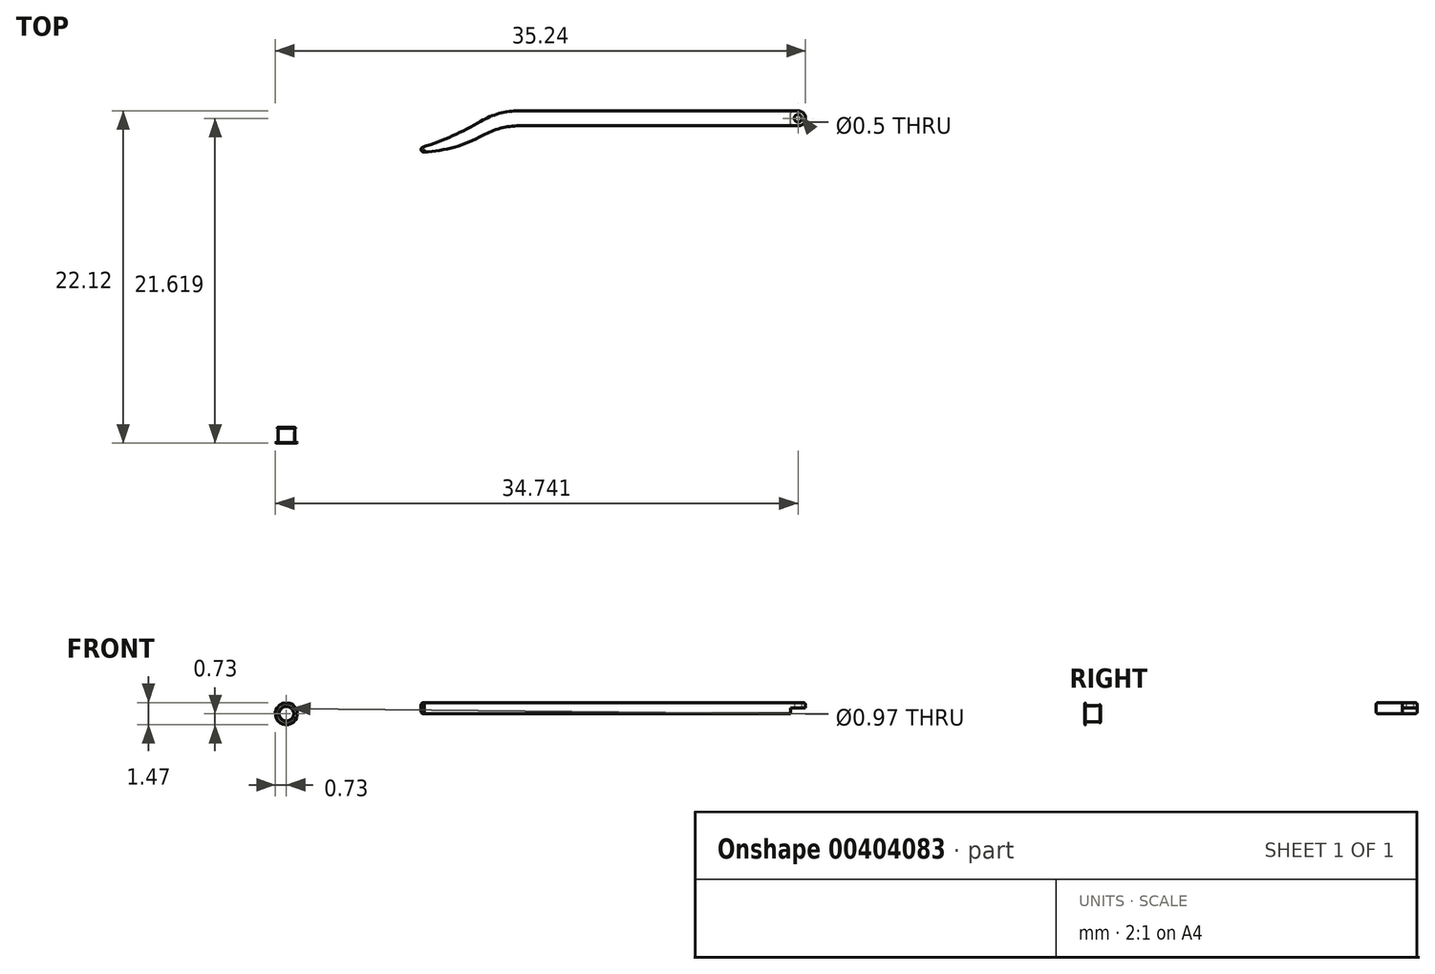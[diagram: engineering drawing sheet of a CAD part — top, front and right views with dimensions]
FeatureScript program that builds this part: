
annotation { "Feature Type Name" : "Feature", "Feature Type Description" : "" }
export const myFeature = defineFeature(function(context is Context, id is Id, definition is map)
    precondition{}
    {
        {
            var Q0;
            Q0=qCreatedBy(makeId("Top.planeOp"),FACE);
            var sketch = newSketch(context, id + "F0", { "sketchPlane" : qUnion([Q0])});
            skLineSegment(sketch, "E0", {"start": v(34.01, 20.71) * mm, "end": v(15.5, 20.71) * mm});
            skLineSegment(sketch, "E1", {"start": v(15.47, 21.7) * mm, "end": v(34.01, 21.7) * mm});
            skArc(sketch, "E2", {"start": v(9.08, 19.3) * mm, "mid": v(9.12, 19.31) * mm, "end": v(9.17, 19.33) * mm});
            skPoint(sketch, "E3.visualSharp", {"position": v(14.01, 21.7) * mm});
            skArc(sketch, "E3.filletArc", {"start": v(15.47, 21.7) * mm, "mid": v(14.15, 21.53) * mm, "end": v(12.92, 21) * mm});
            skArc(sketch, "E4", {"start": v(9.18, 18.97) * mm, "mid": v(11.18, 19.3) * mm, "end": v(13.06, 20.07) * mm});
            skArc(sketch, "E5.filletArc", {"start": v(15.5, 20.71) * mm, "mid": v(14.24, 20.55) * mm, "end": v(13.06, 20.07) * mm});
            skLineSegment(sketch, "E6", {"start": v(9.08, 19.3) * mm, "end": v(9.13, 19.13) * mm, "construction": true});
            skLineSegment(sketch, "E7", {"start": v(9.13, 19.13) * mm, "end": v(9.18, 18.97) * mm, "construction": true});
            skArc(sketch, "E8", {"start": v(34.01, 20.71) * mm, "mid": v(34.5, 21.2) * mm, "end": v(34.01, 21.7) * mm});
            skArc(sketch, "E9", {"start": v(9.08, 19.3) * mm, "mid": v(8.96, 19.08) * mm, "end": v(9.18, 18.97) * mm});
            skArc(sketch, "E10", {"start": v(9.17, 19.33) * mm, "mid": v(11.1, 20.06) * mm, "end": v(12.92, 21) * mm});
            skCircle(sketch, "E11", {"center": v(34.01, 21.2) * mm, "radius": 0.5 * mm});
            skPoint(sketch, "E12.trimOffspring.end.orphan", {"position": v(34.5, 21.2) * mm});
            skPoint(sketch, "E13.orphan", {"position": v(33.96, 21.7) * mm});
            skPoint(sketch, "E14.orphan", {"position": v(34.06, 21.7) * mm});
            skLineSegment(sketch, "E15", {"start": v(33.96, 21.16) * mm, "end": v(34.06, 21.16) * mm});
            skLineSegment(sketch, "E16", {"start": v(34.06, 21.16) * mm, "end": v(34.06, 21.26) * mm});
            skLineSegment(sketch, "E17", {"start": v(33.96, 21.16) * mm, "end": v(33.96, 21.26) * mm});
            skLineSegment(sketch, "E18", {"start": v(33.96, 21.26) * mm, "end": v(34.06, 21.26) * mm});
            skPoint(sketch, "E19", {"position": v(34.06, 21.26) * mm});
            skPoint(sketch, "E20", {"position": v(34.06, 21.16) * mm});
            skPoint(sketch, "E21", {"position": v(33.96, 21.16) * mm});
            skPoint(sketch, "E22", {"position": v(33.96, 21.26) * mm});
            skPoint(sketch, "E23.end.orphan", {"position": v(33.96, 21.1) * mm});
            skLineSegment(sketch, "E24", {"start": v(34.06, 21.26) * mm, "end": v(34.06, 21.53) * mm});
            skLineSegment(sketch, "E25", {"start": v(33.96, 21.26) * mm, "end": v(33.96, 21.53) * mm});
            skLineSegment(sketch, "E26", {"start": v(34.06, 21.26) * mm, "end": v(34.33, 21.26) * mm});
            skLineSegment(sketch, "E27", {"start": v(34.06, 21.16) * mm, "end": v(34.33, 21.16) * mm});
            skLineSegment(sketch, "E28", {"start": v(33.96, 21.16) * mm, "end": v(33.7, 21.16) * mm});
            skLineSegment(sketch, "E29", {"start": v(33.96, 21.26) * mm, "end": v(33.7, 21.26) * mm});
            skLineSegment(sketch, "E30", {"start": v(34.06, 21.16) * mm, "end": v(34.06, 20.89) * mm});
            skLineSegment(sketch, "E31", {"start": v(33.96, 21.16) * mm, "end": v(33.96, 20.89) * mm});
            skCircle(sketch, "E32", {"center": v(34.01, 21.2) * mm, "radius": 0.25 * mm});
            skCircle(sketch, "E33", {"center": v(34.01, 21.2) * mm, "radius": 0.32 * mm});
            skSolve(sketch);
        }
        {
            var Q0;
            {var subQ0=sQuery(id+"F0.wireOp",EDGE,"raI6fAfw-WQBC-BWmR-UYK9-M2oQmZqHLvwO");var subQ5=makeQuery(id+"F0.imprint","INTERSECT",VERTEX,{"derivedFrom":[subQ0,sQuery(id+"F0.wireOp",EDGE,"49f3884b-ec54-47d6-9d62-e5366d3701af.trimOffspring")]});Q0=makeQuery(id+"F0.imprint","IMPRINT",FACE,{"disambiguationData":[TD([[makeQuery(id+"F0.imprint","IMPRINT",EDGE,{"disambiguationData":[TD([[subQ5,-1.0]])],"derivedFrom":subQ0}),1.0]])]});}
            var Q1;
            {var subQ0=sQuery(id+"F0.wireOp",EDGE,"byHKuAPP-PSI1-Uxzz-RkZZ-SpkTKzF2PoQ2");Q1=makeQuery(id+"F0.imprint","IMPRINT",FACE,{"disambiguationData":[TD([[makeQuery(id+"F0.imprint","IMPRINT",EDGE,{"derivedFrom":subQ0}),1.0]])]});}
            var Q2;
            {var subQ0=sQuery(id+"F0.wireOp",EDGE,"byHKuAPP-PSI1-Uxzz-RkZZ-SpkTKzF2PoQ2");Q2=makeQuery(id+"F0.imprint","IMPRINT",FACE,{"disambiguationData":[TD([[makeQuery(id+"F0.imprint","IMPRINT",EDGE,{"derivedFrom":subQ0}),-1.0]])]});}
            var Q3;
            {var subQ0=sQuery(id+"F0.wireOp",EDGE,"b7881604-9c53-4a02-ad4f-a8e66866f7ef.trimOffspring");Q3=makeQuery(id+"F0.imprint","IMPRINT",FACE,{"disambiguationData":[TD([[makeQuery(id+"F0.imprint","IMPRINT",EDGE,{"derivedFrom":subQ0}),-1.0]])]});}
            var Q4;
            {var subQ0=sQuery(id+"F0.wireOp",EDGE,"f60c8f39-9fcf-4c3e-999d-d28395edd9ea.trimOffspring");Q4=makeQuery(id+"F0.imprint","IMPRINT",FACE,{"disambiguationData":[TD([[makeQuery(id+"F0.imprint","IMPRINT",EDGE,{"derivedFrom":subQ0}),-1.0]])]});}
            var Q5;
            {var subQ0=sQuery(id+"F0.wireOp",EDGE,"f60c8f39-9fcf-4c3e-999d-d28395edd9ea.trimOffspring");Q5=makeQuery(id+"F0.imprint","IMPRINT",FACE,{"disambiguationData":[TD([[makeQuery(id+"F0.imprint","IMPRINT",EDGE,{"derivedFrom":subQ0}),1.0]])]});}
            var Q6;
            {var subQ0=sQuery(id+"F0.wireOp",EDGE,"49f3884b-ec54-47d6-9d62-e5366d3701af.trimOffspring");Q6=makeQuery(id+"F0.imprint","IMPRINT",FACE,{"disambiguationData":[TD([[makeQuery(id+"F0.imprint","IMPRINT",EDGE,{"derivedFrom":subQ0}),1.0]])]});}
            var Q7;
            {var subQ0=sQuery(id+"F0.wireOp",EDGE,"UlwEkzhg-5pLx-n1i1-Rf2w-oDDQLxGLouVm");Q7=makeQuery(id+"F0.imprint","IMPRINT",FACE,{"disambiguationData":[TD([[makeQuery(id+"F0.imprint","IMPRINT",EDGE,{"derivedFrom":subQ0}),-1.0]])]});}
            var Q8;
            {var subQ0=sQuery(id+"F0.wireOp",EDGE,"UlwEkzhg-5pLx-n1i1-Rf2w-oDDQLxGLouVm");Q8=makeQuery(id+"F0.imprint","IMPRINT",FACE,{"disambiguationData":[TD([[makeQuery(id+"F0.imprint","IMPRINT",EDGE,{"derivedFrom":subQ0}),1.0]])]});}
            var Q9;
            {var subQ4=sQuery(id+"F0.wireOp",EDGE,"E11");var subQ5=makeQuery(id+"F0.imprint","INTERSECT",VERTEX,{"derivedFrom":[sQuery(id+"F0.wireOp",EDGE,"E0"),subQ4]});Q9=makeQuery(id+"F0.imprint","IMPRINT",FACE,{"disambiguationData":[TD([[makeQuery(id+"F0.imprint","IMPRINT",EDGE,{"disambiguationData":[TD([[subQ5,1.0]])],"derivedFrom":subQ4}),1.0]])]});}
            var Q10;
            {var subQ1=sQuery(id+"F0.wireOp",EDGE,"E0");Q10=makeQuery(id+"F0.imprint","IMPRINT",FACE,{"disambiguationData":[TD([[makeQuery(id+"F0.imprint","IMPRINT",EDGE,{"derivedFrom":subQ1}),-1.0]])]});}
            var Q11;
            Q11=makeQuery(id+"F0.imprint","IMPRINT",FACE,{"disambiguationData":[TD([[makeQuery(id+"F0.imprint","IMPRINT",EDGE,{"derivedFrom":sQuery(id+"F0.wireOp",EDGE,"xuiiaQj0-0Hdb-vT5L-Vz9f-apvYOn73sIt9")}),1.0]])]});
            var Q12;
            {var subQ0=sQuery(id+"F0.wireOp",EDGE,"8bITlogX-qrIG-J57A-UWLq-Q11sDlbSrRPg");Q12=makeQuery(id+"F0.imprint","IMPRINT",FACE,{"disambiguationData":[TD([[makeQuery(id+"F0.imprint","IMPRINT",EDGE,{"derivedFrom":subQ0}),1.0]])]});}
            var Q13;
            {var subQ2=sQuery(id+"F0.wireOp",EDGE,"CakERchI-l42z-6pcw-9BF8-LHwAbAGrC5tK");Q13=makeQuery(id+"F0.imprint","IMPRINT",FACE,{"disambiguationData":[TD([[makeQuery(id+"F0.imprint","IMPRINT",EDGE,{"derivedFrom":subQ2}),1.0]])]});}
            var Q14;
            {var subQ0=sQuery(id+"F0.wireOp",EDGE,"wC2ZcHAF-Bbkc-jGNR-qgdj-bPsWVvPjC4N5");Q14=makeQuery(id+"F0.imprint","IMPRINT",FACE,{"disambiguationData":[TD([[makeQuery(id+"F0.imprint","IMPRINT",EDGE,{"derivedFrom":subQ0}),1.0]])]});}
            var Q15;
            {var subQ2=sQuery(id+"F0.wireOp",EDGE,"E23");Q15=makeQuery(id+"F0.imprint","IMPRINT",FACE,{"disambiguationData":[TD([[makeQuery(id+"F0.imprint","IMPRINT",EDGE,{"derivedFrom":subQ2}),1.0]])]});}
            var Q16;
            {var subQ0=sQuery(id+"F0.wireOp",EDGE,"j64aIYXc-tMoq-sI7k-U2CT-7rPPRVJO4i3e");Q16=makeQuery(id+"F0.imprint","IMPRINT",FACE,{"disambiguationData":[TD([[makeQuery(id+"F0.imprint","IMPRINT",EDGE,{"derivedFrom":subQ0}),1.0]])]});}
            var Q17;
            {var subQ2=sQuery(id+"F0.wireOp",EDGE,"j64aIYXc-tMoq-sI7k-U2CT-7rPPRVJO4i3e");Q17=makeQuery(id+"F0.imprint","IMPRINT",FACE,{"disambiguationData":[TD([[makeQuery(id+"F0.imprint","IMPRINT",EDGE,{"derivedFrom":subQ2}),-1.0]])]});}
            var Q18;
            {var subQ0=sQuery(id+"F0.wireOp",EDGE,"GzgODX0R-oJ5M-ROGA-YiOL-rSwiiqXDl5Cg");Q18=makeQuery(id+"F0.imprint","IMPRINT",FACE,{"disambiguationData":[TD([[makeQuery(id+"F0.imprint","IMPRINT",EDGE,{"derivedFrom":subQ0}),-1.0]])]});}
            var Q19;
            {var subQ0=sQuery(id+"F0.wireOp",EDGE,"E28");var subQ1=sQuery(id+"F0.wireOp",EDGE,"E11");var subQ2=makeQuery(id+"F0.imprint","INTERSECT",VERTEX,{"derivedFrom":[subQ1,subQ0]});Q19=makeQuery(id+"F0.imprint","IMPRINT",FACE,{"disambiguationData":[TD([[makeQuery(id+"F0.imprint","IMPRINT",EDGE,{"disambiguationData":[TD([[subQ2,-1.0]])],"derivedFrom":subQ1}),1.0]])]});}
            var Q20;
            {var subQ0=sQuery(id+"F0.wireOp",EDGE,"E28");var subQ1=sQuery(id+"F0.wireOp",EDGE,"E11");var subQ2=makeQuery(id+"F0.imprint","INTERSECT",VERTEX,{"derivedFrom":[subQ1,subQ0]});Q20=makeQuery(id+"F0.imprint","IMPRINT",FACE,{"disambiguationData":[TD([[makeQuery(id+"F0.imprint","IMPRINT",EDGE,{"disambiguationData":[TD([[subQ2,1.0]])],"derivedFrom":subQ1}),1.0]])]});}
            var Q21;
            {var subQ0=sQuery(id+"F0.wireOp",EDGE,"E25");var subQ1=sQuery(id+"F0.wireOp",EDGE,"E11");var subQ2=makeQuery(id+"F0.imprint","INTERSECT",VERTEX,{"derivedFrom":[subQ1,subQ0]});Q21=makeQuery(id+"F0.imprint","IMPRINT",FACE,{"disambiguationData":[TD([[makeQuery(id+"F0.imprint","IMPRINT",EDGE,{"disambiguationData":[TD([[subQ2,-1.0]])],"derivedFrom":subQ1}),1.0]])]});}
            var Q22;
            {var subQ0=sQuery(id+"F0.wireOp",EDGE,"E25");var subQ1=sQuery(id+"F0.wireOp",EDGE,"kEdUQFwA-TB42-oZai-H7MF-9FTqb3vRD3eQ");var subQ2=makeQuery(id+"F0.imprint","INTERSECT",VERTEX,{"derivedFrom":[subQ1,subQ0]});Q22=makeQuery(id+"F0.imprint","IMPRINT",FACE,{"disambiguationData":[TD([[makeQuery(id+"F0.imprint","IMPRINT",EDGE,{"disambiguationData":[TD([[subQ2,-1.0]])],"derivedFrom":subQ1}),-1.0]])]});}
            var Q23;
            {var subQ0=sQuery(id+"F0.wireOp",EDGE,"E29");var subQ1=sQuery(id+"F0.wireOp",EDGE,"kEdUQFwA-TB42-oZai-H7MF-9FTqb3vRD3eQ");var subQ2=makeQuery(id+"F0.imprint","INTERSECT",VERTEX,{"derivedFrom":[subQ1,subQ0]});Q23=makeQuery(id+"F0.imprint","IMPRINT",FACE,{"disambiguationData":[TD([[makeQuery(id+"F0.imprint","IMPRINT",EDGE,{"disambiguationData":[TD([[subQ2,-1.0]])],"derivedFrom":subQ1}),-1.0]])]});}
            var Q24;
            {var subQ0=sQuery(id+"F0.wireOp",EDGE,"E28");var subQ1=sQuery(id+"F0.wireOp",EDGE,"kEdUQFwA-TB42-oZai-H7MF-9FTqb3vRD3eQ");var subQ2=makeQuery(id+"F0.imprint","INTERSECT",VERTEX,{"derivedFrom":[subQ1,subQ0]});Q24=makeQuery(id+"F0.imprint","IMPRINT",FACE,{"disambiguationData":[TD([[makeQuery(id+"F0.imprint","IMPRINT",EDGE,{"disambiguationData":[TD([[subQ2,-1.0]])],"derivedFrom":subQ1}),-1.0]])]});}
            var Q25;
            {var subQ0=sQuery(id+"F0.wireOp",EDGE,"E25");var subQ1=sQuery(id+"F0.wireOp",EDGE,"kEdUQFwA-TB42-oZai-H7MF-9FTqb3vRD3eQ");var subQ2=makeQuery(id+"F0.imprint","INTERSECT",VERTEX,{"derivedFrom":[subQ1,subQ0]});Q25=makeQuery(id+"F0.imprint","IMPRINT",FACE,{"disambiguationData":[TD([[makeQuery(id+"F0.imprint","IMPRINT",EDGE,{"disambiguationData":[TD([[subQ2,-1.0]])],"derivedFrom":subQ1}),1.0]])]});}
            var Q26;
            {var subQ5=sQuery(id+"F0.wireOp",EDGE,"E17");Q26=makeQuery(id+"F0.imprint","IMPRINT",FACE,{"disambiguationData":[TD([[makeQuery(id+"F0.imprint","IMPRINT",EDGE,{"derivedFrom":subQ5}),1.0]])]});}
            var Q27;
            {var subQ0=sQuery(id+"F0.wireOp",EDGE,"E28");var subQ1=sQuery(id+"F0.wireOp",EDGE,"kEdUQFwA-TB42-oZai-H7MF-9FTqb3vRD3eQ");var subQ2=makeQuery(id+"F0.imprint","INTERSECT",VERTEX,{"derivedFrom":[subQ1,subQ0]});Q27=makeQuery(id+"F0.imprint","IMPRINT",FACE,{"disambiguationData":[TD([[makeQuery(id+"F0.imprint","IMPRINT",EDGE,{"disambiguationData":[TD([[subQ2,-1.0]])],"derivedFrom":subQ1}),1.0]])]});}
            var Q28;
            {var subQ5=sQuery(id+"F0.wireOp",EDGE,"E11");var subQ6=makeQuery(id+"F0.imprint","INTERSECT",VERTEX,{"derivedFrom":[sQuery(id+"F0.wireOp",EDGE,"E1"),subQ5]});Q28=makeQuery(id+"F0.imprint","IMPRINT",FACE,{"disambiguationData":[TD([[makeQuery(id+"F0.imprint","IMPRINT",EDGE,{"disambiguationData":[TD([[subQ6,1.0]])],"derivedFrom":subQ5}),1.0]])]});}
            var Q29;
            {var subQ0=sQuery(id+"F0.wireOp",EDGE,"E24");var subQ1=sQuery(id+"F0.wireOp",EDGE,"kEdUQFwA-TB42-oZai-H7MF-9FTqb3vRD3eQ");var subQ2=makeQuery(id+"F0.imprint","INTERSECT",VERTEX,{"derivedFrom":[subQ1,subQ0]});Q29=makeQuery(id+"F0.imprint","IMPRINT",FACE,{"disambiguationData":[TD([[makeQuery(id+"F0.imprint","IMPRINT",EDGE,{"disambiguationData":[TD([[subQ2,-1.0]])],"derivedFrom":subQ1}),-1.0]])]});}
            var Q30;
            {var subQ5=sQuery(id+"F0.wireOp",EDGE,"E18");Q30=makeQuery(id+"F0.imprint","IMPRINT",FACE,{"disambiguationData":[TD([[makeQuery(id+"F0.imprint","IMPRINT",EDGE,{"derivedFrom":subQ5}),1.0]])]});}
            var Q31;
            Q31=makeQuery(id+"F0.imprint","IMPRINT",FACE,{"disambiguationData":[TD([[makeQuery(id+"F0.imprint","IMPRINT",EDGE,{"derivedFrom":sQuery(id+"F0.wireOp",EDGE,"E15")}),1.0]])]});
            var Q32;
            {var subQ5=sQuery(id+"F0.wireOp",EDGE,"E15");Q32=makeQuery(id+"F0.imprint","IMPRINT",FACE,{"disambiguationData":[TD([[makeQuery(id+"F0.imprint","IMPRINT",EDGE,{"derivedFrom":subQ5}),-1.0]])]});}
            var Q33;
            {var subQ0=sQuery(id+"F0.wireOp",EDGE,"E31");var subQ1=sQuery(id+"F0.wireOp",EDGE,"kEdUQFwA-TB42-oZai-H7MF-9FTqb3vRD3eQ");var subQ2=makeQuery(id+"F0.imprint","INTERSECT",VERTEX,{"derivedFrom":[subQ1,subQ0]});Q33=makeQuery(id+"F0.imprint","IMPRINT",FACE,{"disambiguationData":[TD([[makeQuery(id+"F0.imprint","IMPRINT",EDGE,{"disambiguationData":[TD([[subQ2,-1.0]])],"derivedFrom":subQ1}),-1.0]])]});}
            var Q34;
            {var subQ0=sQuery(id+"F0.wireOp",EDGE,"E24");var subQ1=sQuery(id+"F0.wireOp",EDGE,"E11");var subQ2=makeQuery(id+"F0.imprint","INTERSECT",VERTEX,{"derivedFrom":[subQ1,subQ0]});Q34=makeQuery(id+"F0.imprint","IMPRINT",FACE,{"disambiguationData":[TD([[makeQuery(id+"F0.imprint","IMPRINT",EDGE,{"disambiguationData":[TD([[subQ2,1.0]])],"derivedFrom":subQ1}),1.0]])]});}
            var Q35;
            {var subQ0=sQuery(id+"F0.wireOp",EDGE,"E24");var subQ1=sQuery(id+"F0.wireOp",EDGE,"kEdUQFwA-TB42-oZai-H7MF-9FTqb3vRD3eQ");var subQ2=makeQuery(id+"F0.imprint","INTERSECT",VERTEX,{"derivedFrom":[subQ1,subQ0]});Q35=makeQuery(id+"F0.imprint","IMPRINT",FACE,{"disambiguationData":[TD([[makeQuery(id+"F0.imprint","IMPRINT",EDGE,{"disambiguationData":[TD([[subQ2,1.0]])],"derivedFrom":subQ1}),-1.0]])]});}
            var Q36;
            {var subQ5=sQuery(id+"F0.wireOp",EDGE,"E16");Q36=makeQuery(id+"F0.imprint","IMPRINT",FACE,{"disambiguationData":[TD([[makeQuery(id+"F0.imprint","IMPRINT",EDGE,{"derivedFrom":subQ5}),-1.0]])]});}
            var Q37;
            {var subQ0=sQuery(id+"F0.wireOp",EDGE,"E30");var subQ1=sQuery(id+"F0.wireOp",EDGE,"kEdUQFwA-TB42-oZai-H7MF-9FTqb3vRD3eQ");var subQ2=makeQuery(id+"F0.imprint","INTERSECT",VERTEX,{"derivedFrom":[subQ1,subQ0]});Q37=makeQuery(id+"F0.imprint","IMPRINT",FACE,{"disambiguationData":[TD([[makeQuery(id+"F0.imprint","IMPRINT",EDGE,{"disambiguationData":[TD([[subQ2,-1.0]])],"derivedFrom":subQ1}),1.0]])]});}
            var Q38;
            {var subQ0=sQuery(id+"F0.wireOp",EDGE,"E30");var subQ1=sQuery(id+"F0.wireOp",EDGE,"kEdUQFwA-TB42-oZai-H7MF-9FTqb3vRD3eQ");var subQ2=makeQuery(id+"F0.imprint","INTERSECT",VERTEX,{"derivedFrom":[subQ1,subQ0]});Q38=makeQuery(id+"F0.imprint","IMPRINT",FACE,{"disambiguationData":[TD([[makeQuery(id+"F0.imprint","IMPRINT",EDGE,{"disambiguationData":[TD([[subQ2,-1.0]])],"derivedFrom":subQ1}),-1.0]])]});}
            var Q39;
            {var subQ0=sQuery(id+"F0.wireOp",EDGE,"E27");var subQ1=sQuery(id+"F0.wireOp",EDGE,"E11");var subQ2=makeQuery(id+"F0.imprint","INTERSECT",VERTEX,{"derivedFrom":[subQ1,subQ0]});Q39=makeQuery(id+"F0.imprint","IMPRINT",FACE,{"disambiguationData":[TD([[makeQuery(id+"F0.imprint","IMPRINT",EDGE,{"disambiguationData":[TD([[subQ2,1.0]])],"derivedFrom":subQ1}),1.0]])]});}
            var Q40;
            {var subQ0=sQuery(id+"F0.wireOp",EDGE,"E26");var subQ1=sQuery(id+"F0.wireOp",EDGE,"kEdUQFwA-TB42-oZai-H7MF-9FTqb3vRD3eQ");var subQ2=makeQuery(id+"F0.imprint","INTERSECT",VERTEX,{"derivedFrom":[subQ1,subQ0]});Q40=makeQuery(id+"F0.imprint","IMPRINT",FACE,{"disambiguationData":[TD([[makeQuery(id+"F0.imprint","IMPRINT",EDGE,{"disambiguationData":[TD([[subQ2,1.0]])],"derivedFrom":subQ1}),-1.0]])]});}
            var Q41;
            {var subQ0=sQuery(id+"F0.wireOp",EDGE,"E28");var subQ1=sQuery(id+"F0.wireOp",EDGE,"kEdUQFwA-TB42-oZai-H7MF-9FTqb3vRD3eQ");var subQ2=makeQuery(id+"F0.imprint","INTERSECT",VERTEX,{"derivedFrom":[subQ1,subQ0]});Q41=makeQuery(id+"F0.imprint","IMPRINT",FACE,{"disambiguationData":[TD([[makeQuery(id+"F0.imprint","IMPRINT",EDGE,{"disambiguationData":[TD([[subQ2,1.0]])],"derivedFrom":subQ1}),1.0]])]});}
            var Q42;
            {var subQ1=sQuery(id+"F0.wireOp",EDGE,"E28");var subQ3=sQuery(id+"F0.wireOp",EDGE,"E32");var subQ4=makeQuery(id+"F0.imprint","INTERSECT",VERTEX,{"derivedFrom":[subQ1,subQ3]});Q42=makeQuery(id+"F0.imprint","IMPRINT",FACE,{"disambiguationData":[TD([[makeQuery(id+"F0.imprint","IMPRINT",EDGE,{"disambiguationData":[TD([[subQ4,-1.0]])],"derivedFrom":subQ3}),1.0]])]});}
            var Q43;
            {var subQ1=sQuery(id+"F0.wireOp",EDGE,"E25");var subQ3=sQuery(id+"F0.wireOp",EDGE,"E32");var subQ4=makeQuery(id+"F0.imprint","INTERSECT",VERTEX,{"derivedFrom":[subQ1,subQ3]});Q43=makeQuery(id+"F0.imprint","IMPRINT",FACE,{"disambiguationData":[TD([[makeQuery(id+"F0.imprint","IMPRINT",EDGE,{"disambiguationData":[TD([[subQ4,-1.0]])],"derivedFrom":subQ3}),1.0]])]});}
            var Q44;
            {var subQ0=sQuery(id+"F0.wireOp",EDGE,"E24");var subQ1=sQuery(id+"F0.wireOp",EDGE,"kEdUQFwA-TB42-oZai-H7MF-9FTqb3vRD3eQ");var subQ2=makeQuery(id+"F0.imprint","INTERSECT",VERTEX,{"derivedFrom":[subQ1,subQ0]});Q44=makeQuery(id+"F0.imprint","IMPRINT",FACE,{"disambiguationData":[TD([[makeQuery(id+"F0.imprint","IMPRINT",EDGE,{"disambiguationData":[TD([[subQ2,-1.0]])],"derivedFrom":subQ1}),1.0]])]});}
            var Q45;
            {var subQ1=sQuery(id+"F0.wireOp",EDGE,"E27");var subQ3=sQuery(id+"F0.wireOp",EDGE,"E32");var subQ4=makeQuery(id+"F0.imprint","INTERSECT",VERTEX,{"derivedFrom":[subQ1,subQ3]});Q45=makeQuery(id+"F0.imprint","IMPRINT",FACE,{"disambiguationData":[TD([[makeQuery(id+"F0.imprint","IMPRINT",EDGE,{"disambiguationData":[TD([[subQ4,1.0]])],"derivedFrom":subQ3}),1.0]])]});}
            var Q46;
            {var subQ0=sQuery(id+"F0.wireOp",EDGE,"E30");var subQ1=sQuery(id+"F0.wireOp",EDGE,"kEdUQFwA-TB42-oZai-H7MF-9FTqb3vRD3eQ");var subQ2=makeQuery(id+"F0.imprint","INTERSECT",VERTEX,{"derivedFrom":[subQ1,subQ0]});Q46=makeQuery(id+"F0.imprint","IMPRINT",FACE,{"disambiguationData":[TD([[makeQuery(id+"F0.imprint","IMPRINT",EDGE,{"disambiguationData":[TD([[subQ2,1.0]])],"derivedFrom":subQ1}),1.0]])]});}
            var Q47;
            {var subQ1=sQuery(id+"F0.wireOp",EDGE,"E24");var subQ3=sQuery(id+"F0.wireOp",EDGE,"E32");var subQ4=makeQuery(id+"F0.imprint","INTERSECT",VERTEX,{"derivedFrom":[subQ1,subQ3]});Q47=makeQuery(id+"F0.imprint","IMPRINT",FACE,{"disambiguationData":[TD([[makeQuery(id+"F0.imprint","IMPRINT",EDGE,{"disambiguationData":[TD([[subQ4,1.0]])],"derivedFrom":subQ3}),1.0]])]});}
            var Q48;
            {var subQ0=sQuery(id+"F0.wireOp",EDGE,"E24");var subQ1=sQuery(id+"F0.wireOp",EDGE,"kEdUQFwA-TB42-oZai-H7MF-9FTqb3vRD3eQ");var subQ2=makeQuery(id+"F0.imprint","INTERSECT",VERTEX,{"derivedFrom":[subQ1,subQ0]});Q48=makeQuery(id+"F0.imprint","IMPRINT",FACE,{"disambiguationData":[TD([[makeQuery(id+"F0.imprint","IMPRINT",EDGE,{"disambiguationData":[TD([[subQ2,1.0]])],"derivedFrom":subQ1}),1.0]])]});}
            var Q49;
            {var subQ0=sQuery(id+"F0.wireOp",EDGE,"E26");var subQ1=sQuery(id+"F0.wireOp",EDGE,"kEdUQFwA-TB42-oZai-H7MF-9FTqb3vRD3eQ");var subQ2=makeQuery(id+"F0.imprint","INTERSECT",VERTEX,{"derivedFrom":[subQ1,subQ0]});Q49=makeQuery(id+"F0.imprint","IMPRINT",FACE,{"disambiguationData":[TD([[makeQuery(id+"F0.imprint","IMPRINT",EDGE,{"disambiguationData":[TD([[subQ2,1.0]])],"derivedFrom":subQ1}),1.0]])]});}
            var Q50;
            {var subQ0=sQuery(id+"F0.wireOp",EDGE,"E33");var subQ1=sQuery(id+"F0.wireOp",EDGE,"E27");var subQ2=makeQuery(id+"F0.imprint","INTERSECT",VERTEX,{"derivedFrom":[subQ1,subQ0]});Q50=makeQuery(id+"F0.imprint","IMPRINT",FACE,{"disambiguationData":[TD([[makeQuery(id+"F0.imprint","IMPRINT",EDGE,{"disambiguationData":[TD([[subQ2,1.0]])],"derivedFrom":subQ1}),-1.0]])]});}
            var Q51;
            {var subQ0=sQuery(id+"F0.wireOp",EDGE,"E33");var subQ1=sQuery(id+"F0.wireOp",EDGE,"E30");var subQ2=makeQuery(id+"F0.imprint","INTERSECT",VERTEX,{"derivedFrom":[subQ1,subQ0]});Q51=makeQuery(id+"F0.imprint","IMPRINT",FACE,{"disambiguationData":[TD([[makeQuery(id+"F0.imprint","IMPRINT",EDGE,{"disambiguationData":[TD([[subQ2,1.0]])],"derivedFrom":subQ1}),-1.0]])]});}
            var Q52;
            {var subQ0=sQuery(id+"F0.wireOp",EDGE,"E33");var subQ1=sQuery(id+"F0.wireOp",EDGE,"E28");var subQ2=makeQuery(id+"F0.imprint","INTERSECT",VERTEX,{"derivedFrom":[subQ1,subQ0]});Q52=makeQuery(id+"F0.imprint","IMPRINT",FACE,{"disambiguationData":[TD([[makeQuery(id+"F0.imprint","IMPRINT",EDGE,{"disambiguationData":[TD([[subQ2,1.0]])],"derivedFrom":subQ1}),1.0]])]});}
            var Q53;
            {var subQ0=sQuery(id+"F0.wireOp",EDGE,"E33");var subQ1=sQuery(id+"F0.wireOp",EDGE,"E28");var subQ2=makeQuery(id+"F0.imprint","INTERSECT",VERTEX,{"derivedFrom":[subQ1,subQ0]});Q53=makeQuery(id+"F0.imprint","IMPRINT",FACE,{"disambiguationData":[TD([[makeQuery(id+"F0.imprint","IMPRINT",EDGE,{"disambiguationData":[TD([[subQ2,1.0]])],"derivedFrom":subQ1}),-1.0]])]});}
            var Q54;
            {var subQ0=sQuery(id+"F0.wireOp",EDGE,"E33");var subQ1=sQuery(id+"F0.wireOp",EDGE,"E25");var subQ2=makeQuery(id+"F0.imprint","INTERSECT",VERTEX,{"derivedFrom":[subQ1,subQ0]});Q54=makeQuery(id+"F0.imprint","IMPRINT",FACE,{"disambiguationData":[TD([[makeQuery(id+"F0.imprint","IMPRINT",EDGE,{"disambiguationData":[TD([[subQ2,1.0]])],"derivedFrom":subQ1}),1.0]])]});}
            var Q55;
            {var subQ0=sQuery(id+"F0.wireOp",EDGE,"E33");var subQ1=sQuery(id+"F0.wireOp",EDGE,"E24");var subQ2=makeQuery(id+"F0.imprint","INTERSECT",VERTEX,{"derivedFrom":[subQ1,subQ0]});Q55=makeQuery(id+"F0.imprint","IMPRINT",FACE,{"disambiguationData":[TD([[makeQuery(id+"F0.imprint","IMPRINT",EDGE,{"disambiguationData":[TD([[subQ2,1.0]])],"derivedFrom":subQ1}),1.0]])]});}
            var Q56;
            {var subQ0=sQuery(id+"F0.wireOp",EDGE,"E33");var subQ1=sQuery(id+"F0.wireOp",EDGE,"E24");var subQ2=makeQuery(id+"F0.imprint","INTERSECT",VERTEX,{"derivedFrom":[subQ1,subQ0]});Q56=makeQuery(id+"F0.imprint","IMPRINT",FACE,{"disambiguationData":[TD([[makeQuery(id+"F0.imprint","IMPRINT",EDGE,{"disambiguationData":[TD([[subQ2,1.0]])],"derivedFrom":subQ1}),-1.0]])]});}
            var Q57;
            {var subQ0=sQuery(id+"F0.wireOp",EDGE,"E33");var subQ1=sQuery(id+"F0.wireOp",EDGE,"E26");var subQ2=makeQuery(id+"F0.imprint","INTERSECT",VERTEX,{"derivedFrom":[subQ1,subQ0]});Q57=makeQuery(id+"F0.imprint","IMPRINT",FACE,{"disambiguationData":[TD([[makeQuery(id+"F0.imprint","IMPRINT",EDGE,{"disambiguationData":[TD([[subQ2,1.0]])],"derivedFrom":subQ1}),-1.0]])]});}
            extrude(context, id + "F1", {"entities" : qUnion([Q0, Q1, Q2, Q3, Q4, Q5, Q6, Q7, Q8, Q9, Q10, Q11, Q12, Q13, Q14, Q15, Q16, Q17, Q18, Q19, Q20, Q21, Q22, Q23, Q24, Q25, Q26, Q27, Q28, Q29, Q30, Q31, Q32, Q33, Q34, Q35, Q36, Q37, Q38, Q39, Q40, Q41, Q42, Q43, Q44, Q45, Q46, Q47, Q48, Q49, Q50, Q51, Q52, Q53, Q54, Q55, Q56, Q57]), "depth" : .737 * mm, "offsetDistance" : 25 * mm});
        }
        {
            var Q0;
            Q0=makeQuery(id+"Fp0JEHY9HGok3qg_1.opExtrude","CAP_EDGE",EDGE,{"disambiguationData":[OSD([sQuery(id+"F0.wireOp",EDGE,"E11")])],"isStart":false});
            var Q1;
            Q1=makeQuery(id+"F1.opExtrude","CAP_EDGE",EDGE,{"disambiguationData":[OSD([sQuery(id+"F0.wireOp",EDGE,"E0")])],"isStart":true});
            var Q2;
            Q2=makeQuery(id+"F1.opExtrude","CAP_EDGE",EDGE,{"disambiguationData":[OSD([sQuery(id+"F0.wireOp",EDGE,"E9")])],"isStart":true});
            fillet(context, id + "F2", {"entities" : qUnion([Q0, Q1, Q2]), "radius" : 0.15 * mm, "tangentPropagation" : true, "allowEdgeOverflow" : false});
        }
        {
            var Q0;
            Q0=makeQuery(id+"F1.opExtrude","CAP_FACE",FACE,{"disambiguationData":[OSD([sQuery(id+"F0.wireOp",EDGE,"E0"),sQuery(id+"F0.wireOp",EDGE,"E1"),sQuery(id+"F0.wireOp",EDGE,"E2"),sQuery(id+"F0.wireOp",EDGE,"E3.filletArc"),sQuery(id+"F0.wireOp",EDGE,"E4"),sQuery(id+"F0.wireOp",EDGE,"E5.filletArc"),sQuery(id+"F0.wireOp",EDGE,"E9"),sQuery(id+"F0.wireOp",EDGE,"E10"),sQuery(id+"F0.wireOp",EDGE,"E11")])],"isStart":false});
            fillet(context, id + "F3", {"entities" : qUnion([Q0]), "radius" : .15 * mm, "tangentPropagation" : true, "allowEdgeOverflow" : false});
        }
        {
            var Q0;
            {var subQ0=sQuery(id+"F0.wireOp",EDGE,"E33");var subQ1=sQuery(id+"F0.wireOp",EDGE,"E27");var subQ2=makeQuery(id+"F0.imprint","INTERSECT",VERTEX,{"derivedFrom":[subQ1,subQ0]});Q0=makeQuery(id+"F0.imprint","IMPRINT",FACE,{"disambiguationData":[TD([[makeQuery(id+"F0.imprint","IMPRINT",EDGE,{"disambiguationData":[TD([[subQ2,1.0]])],"derivedFrom":subQ1}),-1.0]])]});}
            var Q1;
            {var subQ0=sQuery(id+"F0.wireOp",EDGE,"E33");var subQ1=sQuery(id+"F0.wireOp",EDGE,"E28");var subQ2=makeQuery(id+"F0.imprint","INTERSECT",VERTEX,{"derivedFrom":[subQ1,subQ0]});Q1=makeQuery(id+"F0.imprint","IMPRINT",FACE,{"disambiguationData":[TD([[makeQuery(id+"F0.imprint","IMPRINT",EDGE,{"disambiguationData":[TD([[subQ2,1.0]])],"derivedFrom":subQ1}),1.0]])]});}
            var Q2;
            {var subQ0=sQuery(id+"F0.wireOp",EDGE,"E33");var subQ1=sQuery(id+"F0.wireOp",EDGE,"E25");var subQ2=makeQuery(id+"F0.imprint","INTERSECT",VERTEX,{"derivedFrom":[subQ1,subQ0]});Q2=makeQuery(id+"F0.imprint","IMPRINT",FACE,{"disambiguationData":[TD([[makeQuery(id+"F0.imprint","IMPRINT",EDGE,{"disambiguationData":[TD([[subQ2,1.0]])],"derivedFrom":subQ1}),1.0]])]});}
            var Q3;
            {var subQ0=sQuery(id+"F0.wireOp",EDGE,"E33");var subQ1=sQuery(id+"F0.wireOp",EDGE,"E24");var subQ2=makeQuery(id+"F0.imprint","INTERSECT",VERTEX,{"derivedFrom":[subQ1,subQ0]});Q3=makeQuery(id+"F0.imprint","IMPRINT",FACE,{"disambiguationData":[TD([[makeQuery(id+"F0.imprint","IMPRINT",EDGE,{"disambiguationData":[TD([[subQ2,1.0]])],"derivedFrom":subQ1}),-1.0]])]});}
            extrude(context, id + "F4", {"entities" : qUnion([Q0, Q1, Q2, Q3]), "operationType" : NewBodyOperationType.REMOVE, "oppositeDirection" : true, "depth" : .38 * mm});
        }
        {
            var Q0;
            {var subQ0=sQuery(id+"F0.wireOp",EDGE,"E33");var subQ1=sQuery(id+"F0.wireOp",EDGE,"E32");Q0=makeQuery(id+"F4.boolean.opBoolean","MERGE",FACE,{"derivedFrom":[makeQuery(id+"F1.opExtrude","CAP_FACE",FACE,{"disambiguationData":[OSD([sQuery(id+"F0.wireOp",EDGE,"E0"),sQuery(id+"F0.wireOp",EDGE,"E1"),sQuery(id+"F0.wireOp",EDGE,"E2"),sQuery(id+"F0.wireOp",EDGE,"E3.filletArc"),sQuery(id+"F0.wireOp",EDGE,"E4"),sQuery(id+"F0.wireOp",EDGE,"E5.filletArc"),sQuery(id+"F0.wireOp",EDGE,"E9"),sQuery(id+"F0.wireOp",EDGE,"E10"),sQuery(id+"F0.wireOp",EDGE,"E11")])],"isStart":true}),makeQuery(id+"F4.opExtrude","CAP_FACE",FACE,{"disambiguationData":[OSD([sQuery(id+"F0.wireOp",EDGE,"E24"),sQuery(id+"F0.wireOp",EDGE,"E26"),subQ1,subQ0])],"isStart":true}),makeQuery(id+"F4.opExtrude","CAP_FACE",FACE,{"disambiguationData":[OSD([sQuery(id+"F0.wireOp",EDGE,"E25"),sQuery(id+"F0.wireOp",EDGE,"E29"),subQ1,subQ0])],"isStart":true}),makeQuery(id+"F4.opExtrude","CAP_FACE",FACE,{"disambiguationData":[OSD([sQuery(id+"F0.wireOp",EDGE,"E27"),sQuery(id+"F0.wireOp",EDGE,"E30"),subQ1,subQ0])],"isStart":true}),makeQuery(id+"F4.opExtrude","CAP_FACE",FACE,{"disambiguationData":[OSD([sQuery(id+"F0.wireOp",EDGE,"E28"),sQuery(id+"F0.wireOp",EDGE,"E31"),subQ1,subQ0])],"isStart":true})]});}
            var sketch = newSketch(context, id + "F5", { "sketchPlane" : qUnion([Q0])});
            skCircle(sketch, "E34", {"center": v(34.01, -21.2) * mm, "radius": 0.5 * mm});
            skLineSegment(sketch, "E35", {"start": v(33.51, -20.7) * mm, "end": v(33.51, -21.7) * mm});
            skLineSegment(sketch, "E36", {"start": v(33.51, -21.7) * mm, "end": v(34.01, -21.7) * mm});
            skLineSegment(sketch, "E37", {"start": v(33.51, -20.7) * mm, "end": v(34.01, -20.7) * mm});
            skSolve(sketch);
        }
        {
            var Q0;
            Q0 = qSketchRegion(id + "F5", true);
            extrude(context, id + "F6", {"entities" : qUnion([Q0]), "operationType" : NewBodyOperationType.REMOVE, "oppositeDirection" : true, "depth" : .368 * mm, "offsetDistance" : 25 * mm});
        }
        {
            var Q0;
            Q0=makeQuery(id+"F6.boolean.opBoolean","COPY",FACE,{"derivedFrom":makeQuery(id+"F6.opExtrude","CAP_FACE",FACE,{"disambiguationData":[OSD([sQuery(id+"F5.wireOp",EDGE,"E34")])],"isStart":false})});
            var sketch = newSketch(context, id + "F7", { "sketchPlane" : qUnion([Q0])});
            skCircle(sketch, "E38", {"center": v(34.01, -21.2) * mm, "radius": 0.25 * mm});
            skSolve(sketch);
        }
        {
            var Q0;
            Q0 = qSketchRegion(id + "F7", true);
            extrude(context, id + "F8", {"entities" : qUnion([Q0]), "operationType" : NewBodyOperationType.REMOVE, "endBound" : BoundingType.UP_TO_NEXT, "oppositeDirection" : true, "depth" : 25 * mm, "offsetDistance" : 25 * mm});
        }
        {
            var Q0;
            Q0=qCreatedBy(makeId("Top.planeOp"),FACE);
            var sketch = newSketch(context, id + "F9", { "sketchPlane" : qUnion([Q0])});
            skLineSegment(sketch, "E39", {"start": v(-0.3, 0) * mm, "end": v(0.49, 0) * mm, "construction": true});
            skLineSegment(sketch, "E40", {"start": v(0.49, 0) * mm, "end": v(0.49, 0.65) * mm});
            skArc(sketch, "E41", {"start": v(0.61, 0.61) * mm, "mid": v(0.55, 0.64) * mm, "end": v(0.5, 0.65) * mm});
            skLineSegment(sketch, "E42", {"start": v(0.6, 0.6) * mm, "end": v(0.55, 0.6) * mm});
            skLineSegment(sketch, "E43", {"start": v(0.55, 0.6) * mm, "end": v(0.55, -0.36) * mm});
            skLineSegment(sketch, "E44", {"start": v(0.55, -0.36) * mm, "end": v(0.73, -0.36) * mm});
            skLineSegment(sketch, "E45", {"start": v(0.49, 0) * mm, "end": v(0.49, -0.4) * mm});
            skArc(sketch, "E46", {"start": v(0.5, -0.4) * mm, "mid": v(0.61, -0.4) * mm, "end": v(0.73, -0.37) * mm});
            skPoint(sketch, "E47.visualSharp", {"position": v(0.76, -0.36) * mm});
            skArc(sketch, "E47.filletArc", {"start": v(0.73, -0.37) * mm, "mid": v(0.73, -0.36) * mm, "end": v(0.73, -0.36) * mm});
            skPoint(sketch, "E48.visualSharp", {"position": v(0.62, 0.6) * mm});
            skArc(sketch, "E48.filletArc", {"start": v(0.6, 0.6) * mm, "mid": v(0.61, 0.6) * mm, "end": v(0.61, 0.61) * mm});
            skPoint(sketch, "E49.visualSharp", {"position": v(0.49, 0.65) * mm});
            skArc(sketch, "E49.filletArc", {"start": v(0.5, 0.65) * mm, "mid": v(0.49, 0.65) * mm, "end": v(0.49, 0.65) * mm});
            skPoint(sketch, "E50.visualSharp", {"position": v(0.49, -0.4) * mm});
            skArc(sketch, "E50.filletArc", {"start": v(0.49, -0.4) * mm, "mid": v(0.49, -0.4) * mm, "end": v(0.5, -0.4) * mm});
            skLineSegment(sketch, "E51", {"start": v(0, 0.58) * mm, "end": v(0, -0.46) * mm, "construction": true});
            skSolve(sketch);
        }
        {
            var Q0;
            Q0 = qSketchRegion(id + "F9", true);
            var Q1;
            Q1=sQuery(id+"F9.wireOp",EDGE,"E51");
            revolve(context, id + "F10", {"surfaceOperationType" : NewSurfaceOperationType.NEW, "entities" : qUnion([Q0]), "axis" : qUnion([Q1]), "revolveType" : RevolveType.FULL});
        }
    });
